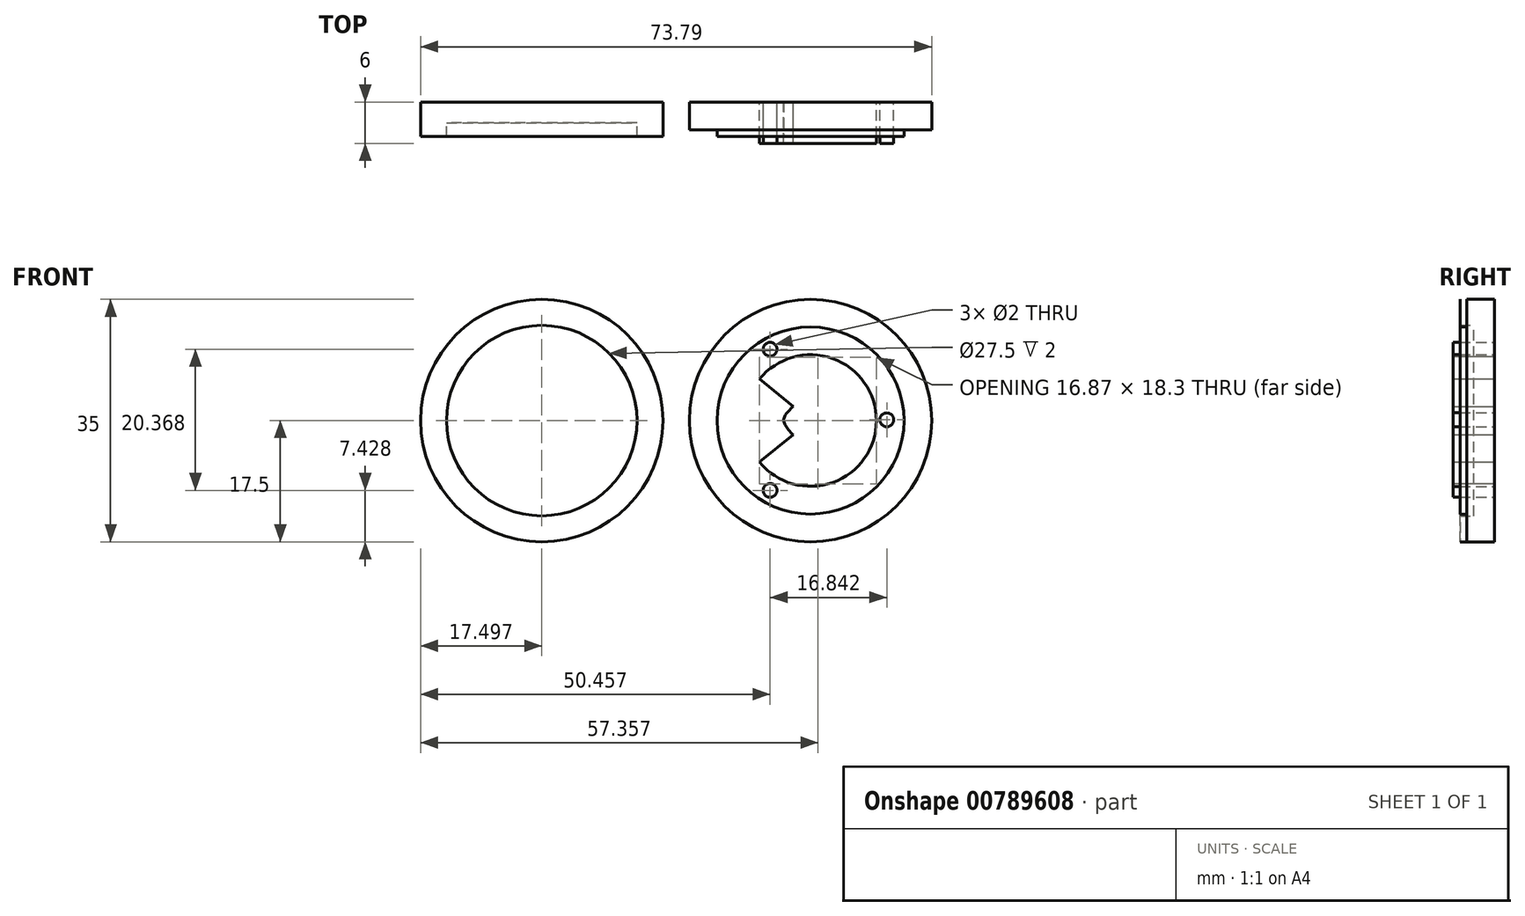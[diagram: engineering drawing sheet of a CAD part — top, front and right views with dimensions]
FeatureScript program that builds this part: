
annotation { "Feature Type Name" : "Feature", "Feature Type Description" : "" }
export const myFeature = defineFeature(function(context is Context, id is Id, definition is map)
    precondition{}
    {
        {
            var Q0;
            Q0=qCreatedBy(makeId("Front.planeOp"),FACE);
            var sketch = newSketch(context, id + "F0", { "sketchPlane" : qUnion([Q0])});
            skCircle(sketch, "E0", {"center": v(0, 0) * mm, "radius": 13.5 * mm});
            skLineSegment(sketch, "E1", {"start": v(-7.37, 6) * mm, "end": v(-2.5, 2.06) * mm});
            skLineSegment(sketch, "E2", {"start": v(-2.5, -2.06) * mm, "end": v(-7.37, -6) * mm});
            skCircle(sketch, "E3", {"center": v(-5.83, -10.07) * mm, "radius": 1 * mm});
            skCircle(sketch, "E4", {"center": v(-5.83, 10.3) * mm, "radius": 1 * mm});
            skFitSpline(sketch, "E5", {"points": [v(-2.5, 2.06) * mm, v(-3.88, 0.11) * mm, v(-2.5, -2.06) * mm], "startDerivative": vector(-3.94, -4.12) * mm, "endDerivative": vector(3.94, -4.12) * mm});
            skCircle(sketch, "E6", {"center": v(11, 0.11) * mm, "radius": 1 * mm});
            skPoint(sketch, "E7", {"position": v(-7.37, 6) * mm});
            skPoint(sketch, "E8", {"position": v(-7.37, -6) * mm});
            skArc(sketch, "E9", {"start": v(-7.37, 6) * mm, "mid": v(9.5, 0) * mm, "end": v(-7.37, -6) * mm});
            skCircle(sketch, "E10", {"center": v(0, 0) * mm, "radius": 17.5 * mm});
            skLineSegment(sketch, "E11", {"start": v(-23.5, 0.11) * mm, "end": v(28.19, 0) * mm, "construction": true});
            skCircle(sketch, "E12", {"center": v(-38.8, 0) * mm, "radius": 13.75 * mm});
            skCircle(sketch, "E13", {"center": v(-38.8, 0) * mm, "radius": 17.5 * mm});
            skSolve(sketch);
        }
        {
            var Q0;
            Q0=makeQuery(id+"F0.imprint","IMPRINT",FACE,{"disambiguationData":[TD([[makeQuery(id+"F0.imprint","IMPRINT",EDGE,{"derivedFrom":sQuery(id+"F0.wireOp",EDGE,"E1")}),1.0]])]});
            var Q1;
            Q1=makeQuery(id+"F0.imprint","IMPRINT",FACE,{"disambiguationData":[TD([[makeQuery(id+"F0.imprint","IMPRINT",EDGE,{"derivedFrom":sQuery(id+"F0.wireOp",EDGE,"E4")}),1.0]])]});
            var Q2;
            Q2=makeQuery(id+"F0.imprint","IMPRINT",FACE,{"disambiguationData":[TD([[makeQuery(id+"F0.imprint","IMPRINT",EDGE,{"derivedFrom":sQuery(id+"F0.wireOp",EDGE,"E3")}),1.0]])]});
            var Q3;
            Q3=makeQuery(id+"F0.imprint","IMPRINT",FACE,{"disambiguationData":[TD([[makeQuery(id+"F0.imprint","IMPRINT",EDGE,{"derivedFrom":sQuery(id+"F0.wireOp",EDGE,"E6")}),1.0]])]});
            extrude(context, id + "F1", {"entities" : qUnion([Q0, Q1, Q2, Q3]), "depth" : 6 * mm, "offsetDistance" : 25 * mm});
        }
        {
            var Q0;
            Q0=makeQuery(id+"F0.imprint","IMPRINT",FACE,{"disambiguationData":[TD([[makeQuery(id+"F0.imprint","IMPRINT",EDGE,{"derivedFrom":sQuery(id+"F0.wireOp",EDGE,"E0")}),1.0]])]});
            extrude(context, id + "F2", {"entities" : qUnion([Q0]), "depth" : 5 * mm, "offsetDistance" : 25 * mm});
        }
        {
            var Q0;
            Q0=makeQuery(id+"F0.imprint","IMPRINT",FACE,{"disambiguationData":[TD([[makeQuery(id+"F0.imprint","IMPRINT",EDGE,{"derivedFrom":sQuery(id+"F0.wireOp",EDGE,"E0")}),-1.0]])]});
            extrude(context, id + "F3", {"entities" : qUnion([Q0]), "operationType" : NewBodyOperationType.ADD, "depth" : 4 * mm, "offsetDistance" : 25 * mm});
        }
        {
            var Q0;
            Q0=makeQuery(id+"F0.imprint","IMPRINT",FACE,{"disambiguationData":[TD([[makeQuery(id+"F0.imprint","IMPRINT",EDGE,{"derivedFrom":sQuery(id+"F0.wireOp",EDGE,"E12")}),1.0]])]});
            extrude(context, id + "F4", {"entities" : qUnion([Q0]), "depth" : 3 * mm, "offsetDistance" : 25 * mm});
        }
        {
            var Q0;
            Q0=makeQuery(id+"F0.imprint","IMPRINT",FACE,{"disambiguationData":[TD([[makeQuery(id+"F0.imprint","IMPRINT",EDGE,{"derivedFrom":sQuery(id+"F0.wireOp",EDGE,"E12")}),-1.0]])]});
            extrude(context, id + "F5", {"entities" : qUnion([Q0]), "operationType" : NewBodyOperationType.ADD, "depth" : 5 * mm, "offsetDistance" : 25 * mm});
        }
    });
